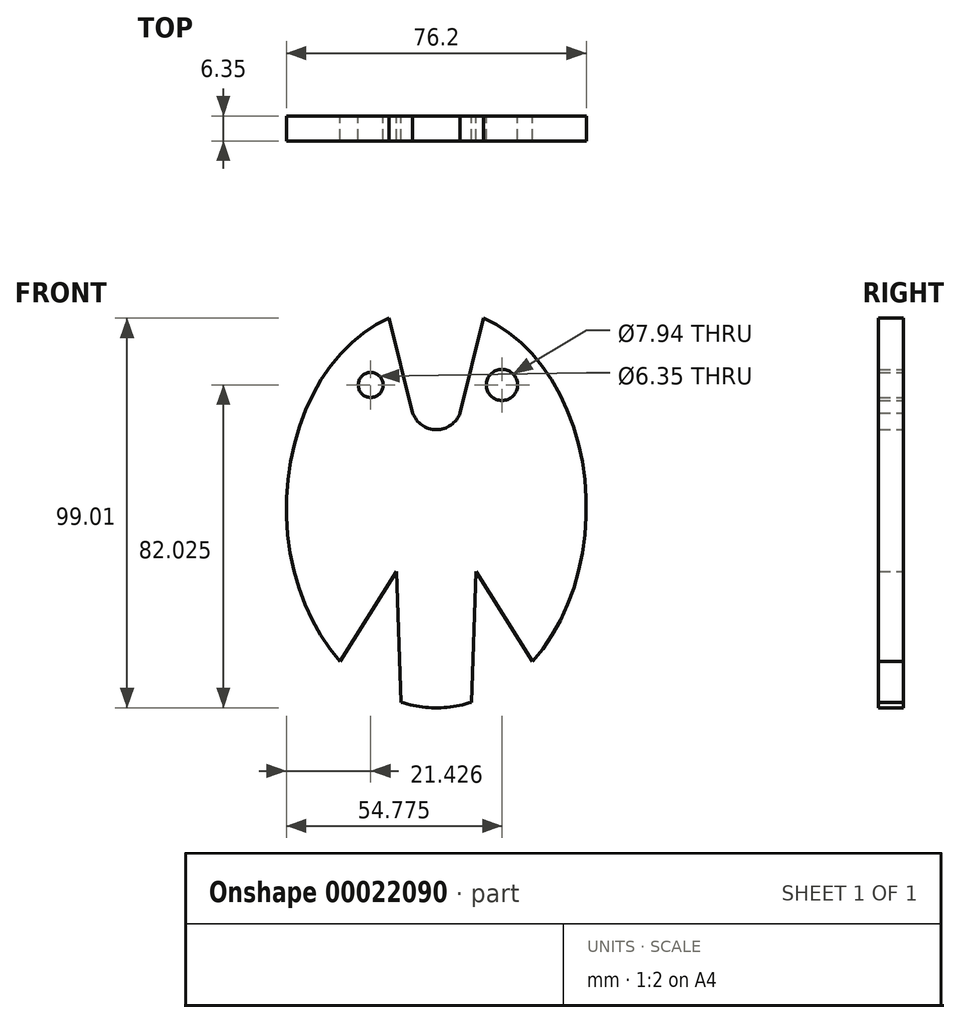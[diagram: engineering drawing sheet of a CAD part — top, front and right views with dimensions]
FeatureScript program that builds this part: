
annotation { "Feature Type Name" : "Feature", "Feature Type Description" : "" }
export const myFeature = defineFeature(function(context is Context, id is Id, definition is map)
    precondition{}
    {
        {
            var Q0;
            Q0=qCreatedBy(makeId("Front.planeOp"),FACE);
            var sketch = newSketch(context, id + "F0", { "sketchPlane" : qUnion([Q0])});
            skEllipticalArc(sketch, "E0", {});
            skLineSegment(sketch, "E1", {"start": v(-6, 24.1) * mm, "end": v(-12.02, 48.2) * mm});
            skLineSegment(sketch, "E2", {"start": v(6, 24.1) * mm, "end": v(12.02, 48.2) * mm});
            skLineSegment(sketch, "E3", {"start": v(-24.43, -38.98) * mm, "end": v(-10.12, -16.14) * mm});
            skLineSegment(sketch, "E4", {"start": v(10.12, -16.14) * mm, "end": v(24.43, -38.98) * mm});
            skLineSegment(sketch, "E5", {"start": v(-10.12, -16.14) * mm, "end": v(-8.89, -50.66) * mm});
            skLineSegment(sketch, "E6", {"start": v(10.12, -16.14) * mm, "end": v(8.9, -50.66) * mm});
            skCircle(sketch, "E7", {"center": v(16.67, 31.22) * mm, "radius": 3.97 * mm});
            skCircle(sketch, "E8", {"center": v(-16.67, 31.22) * mm, "radius": 3.18 * mm});
            skEllipticalArc(sketch, "E9.trimOffspring", {});
            skEllipticalArc(sketch, "E10.trimOffspring", {});
            skArc(sketch, "E11", {"start": v(-6, 24.1) * mm, "mid": v(0, 19.88) * mm, "end": v(6, 24.1) * mm});
            const initialGuessF0  = {"E0": [0, 0, 0, 1, 0.0508, 0.0381, 2.9048645697821494, 3.3783207623805858], "E9.trimOffspring": [0, 0, 0, 1, 0.0508, 0.0381, 3.837699297472408, 5.96226599536062], "E10.trimOffspring": [0, 0, 0, 1, 0.0508, 0.0381, 0.32091928962216637, 2.445486024302078]};
            skSetInitialGuess(sketch, initialGuessF0);
            skSolve(sketch);
        }
        {
            var Q0;
            {var subQ2=sQuery(id+"F0.wireOp",EDGE,"E0");Q0=makeQuery(id+"F0.imprint","IMPRINT",FACE,{"disambiguationData":[TD([[makeQuery(id+"F0.imprint","IMPRINT",EDGE,{"derivedFrom":subQ2}),1.0]])]});}
            extrude(context, id + "F1", {"entities" : qUnion([Q0]), "depth" : 6.35 * mm});
        }
    });
